# Revit family: Deck-mounted mixer sensor tap-Presto  Volta-55252
name_source: partatom
category: Appareils sanitaires
revit_build: Autodesk Revit 2016 (Build: 20150220_1215(x64)
units: mm (PartAtom-declared; Revit-internal decimal feet)

## family parameters
Cote de connecteur circulaire = Utiliser le diamètre
Couper avec des vides une fois chargée = Non
Hôte = Face
Numéro OmniClass = 23.45.55.14
Partagée = Non
Point de calcul de pièce = Non
Titre OmniClass = Single Faucets
Type d'élément = Normal

## types (1)
- Deck-mounted mixer sensor tap-Presto  Volta-55252
    BIMobject category = Sanitary
    CW Inlet = 10 mm  [stored 0.0328084 ft]
    CW Inlet (") = G 3/8"
    Date of publishing = 2011-11-10
    Description = PRESTO VOLTA Deck-mounted mixer sensor tap
    Design country = France
    Edition number = 1
    Elévation par défaut = 1219 mm
    Energy supply = Integrated 6V CRP2 lithium battery
    Fabricant = PRESTO LES ROBINETS
    Flow(With Integrated Flow Limiter) = 2 l/min
    HW Inlet = 10 mm  [stored 0.0328084 ft]
    HW Inlet (") = G 3/8"
    IFC Classification = Space Heater
    Manufacturer country = France
    Manufacturer name = Presto
    Material main = Chrome
    Material secondary = Chrome
    Modèle = 55252
    Nominal height = 0.00
    Nominal width = 0.00
    Operating Pressure = 1 to 5 bar
    Product Guid = 1e3888a1-90c4-42e3-b96e-0d882b256954
    Product SKU = 55252
    Product data url = http://bimobject.com
    Product family = Mixer Sensor Tap
    Product group = Deck-mounted
    QR code = http://bimobject.com
    Temp - Resistance(30 minute Thermal Shock) = 75 °C
    UNSPSC Code = 301815
    Warranty = 3
    Weight Net (Kg) = 0

note: [stored X ft] marks values corroborated as IEEE doubles in the binary element streams (Revit-internal decimal feet)

## geometry (parser evidence)
native form markers: Sweep x8
no freeform markers — native parametric forms only
